# Revit family: 306_02719a1ac9494141afc4109762ffb6
name_source: partatom
category: Pipe Accessories
units: mm (PartAtom-declared; Revit-internal decimal feet)

## family parameters
Always vertical = Yes
Cut with Voids When Loaded = No
Part Type = Valve - Breaks Into
Round Connector Dimension = Use Diameter
Shared = No
Work Plane-Based = No

## types (2) — shared parameters
Description = 3-way Motorized ball valve MBA135, PN32 2x internal/external thread
H1 = 1 mm  [stored 0.00328084 ft]
L2D_Min = 3048 mm
MC = No
Manufacturer = ESBE
QmdConnectorList = 301;D;302;D
URL = http://www.esbe.eu
X5 = 2 mm  [stored 0.00656168 ft]
Y0 = 5 mm  [stored 0.0164042 ft]
Y11 = 3 mm  [stored 0.00984252 ft]
Z3 = 11 mm
Z4 = 52 mm
Z6 = 35 mm
Z6__ve = -35 mm
Z7 = 3 mm  [stored 0.00984252 ft]
magiPartTypeId = 306
magiProductFamilyId = 02719a1ac9494141afc4109762ffb6

## per-type parameters (varying)
- MBA135 G1  FFM 230VAC 2-P 10NM: CenSd_Y10_6=17 mm; D=25 mm; E=29 mm  [stored 0.0951444 ft]; G=76 mm; H=41 mm; L2D=81 mm; W2D=25 mm  [stored 0.082021 ft]; X1=41 mm; X11=27 mm; X11__ve=-27 mm; X12=15 mm  [stored 0.0492126 ft]; X12__ve=-15 mm  [stored -0.0492126 ft]; X14=41 mm; X15=40 mm  [stored 0.131234 ft]; X6=4 mm  [stored 0.0131234 ft]; X7=7 mm  [stored 0.0229659 ft]; X8=20 mm  [stored 0.0656168 ft]; Y1=13 mm  [stored 0.0426509 ft]; Y10=20 mm  [stored 0.0656168 ft]; Y10__ve=-20 mm  [stored -0.0656168 ft]; Y12=12 mm  [stored 0.0393701 ft]; Y2=13 mm  [stored 0.0426509 ft]; Y3=14 mm  [stored 0.0459318 ft]; Y4=15 mm  [stored 0.0492126 ft]; Y5=16 mm; Z10=33 mm; Z2=26 mm; Z2__ve=-26 mm; Z5=3 mm  [stored 0.00984252 ft]; Z9=17 mm; magiProductCode=MBA135 G1" FFM 230VAC 2-P 10NM; magiProductId=4d888fdd6c514516be882b4352fa0c
- MBA135 G3/4  FFM 230VAC 2-P 10NM: CenSd_Y10_6=14 mm  [stored 0.0459318 ft]; D=20 mm; E=25 mm  [stored 0.082021 ft]; G=70 mm; H=34 mm; L2D=68 mm; W2D=20 mm  [stored 0.0656168 ft]; X1=34 mm; X11=22 mm; X11__ve=-22 mm; X12=13 mm  [stored 0.0426509 ft]; X12__ve=-13 mm  [stored -0.0426509 ft]; X14=34 mm; X15=33 mm; X6=3 mm  [stored 0.00984252 ft]; X7=6 mm  [stored 0.019685 ft]; X8=17 mm; Y1=10 mm  [stored 0.0328084 ft]; Y10=16 mm; Y10__ve=-16 mm  [stored -0.0524934 ft]; Y12=10 mm  [stored 0.0328084 ft]; Y2=10 mm  [stored 0.0328084 ft]; Y3=11 mm; Y4=12 mm  [stored 0.0393701 ft]; Y5=12 mm  [stored 0.0393701 ft]; Z10=31 mm  [stored 0.101706 ft]; Z2=23 mm; Z2__ve=-23 mm; Z5=2 mm  [stored 0.00656168 ft]; Z9=16 mm; magiProductCode=MBA135 G3/4" FFM 230VAC 2-P 10NM; magiProductId=a65a2436a2ec4347a39644f3e8380c

note: [stored X ft] marks values corroborated as IEEE doubles in the binary element streams (Revit-internal decimal feet)

## geometry (parser evidence)
native form markers: Sweep x2
no freeform markers — native parametric forms only
